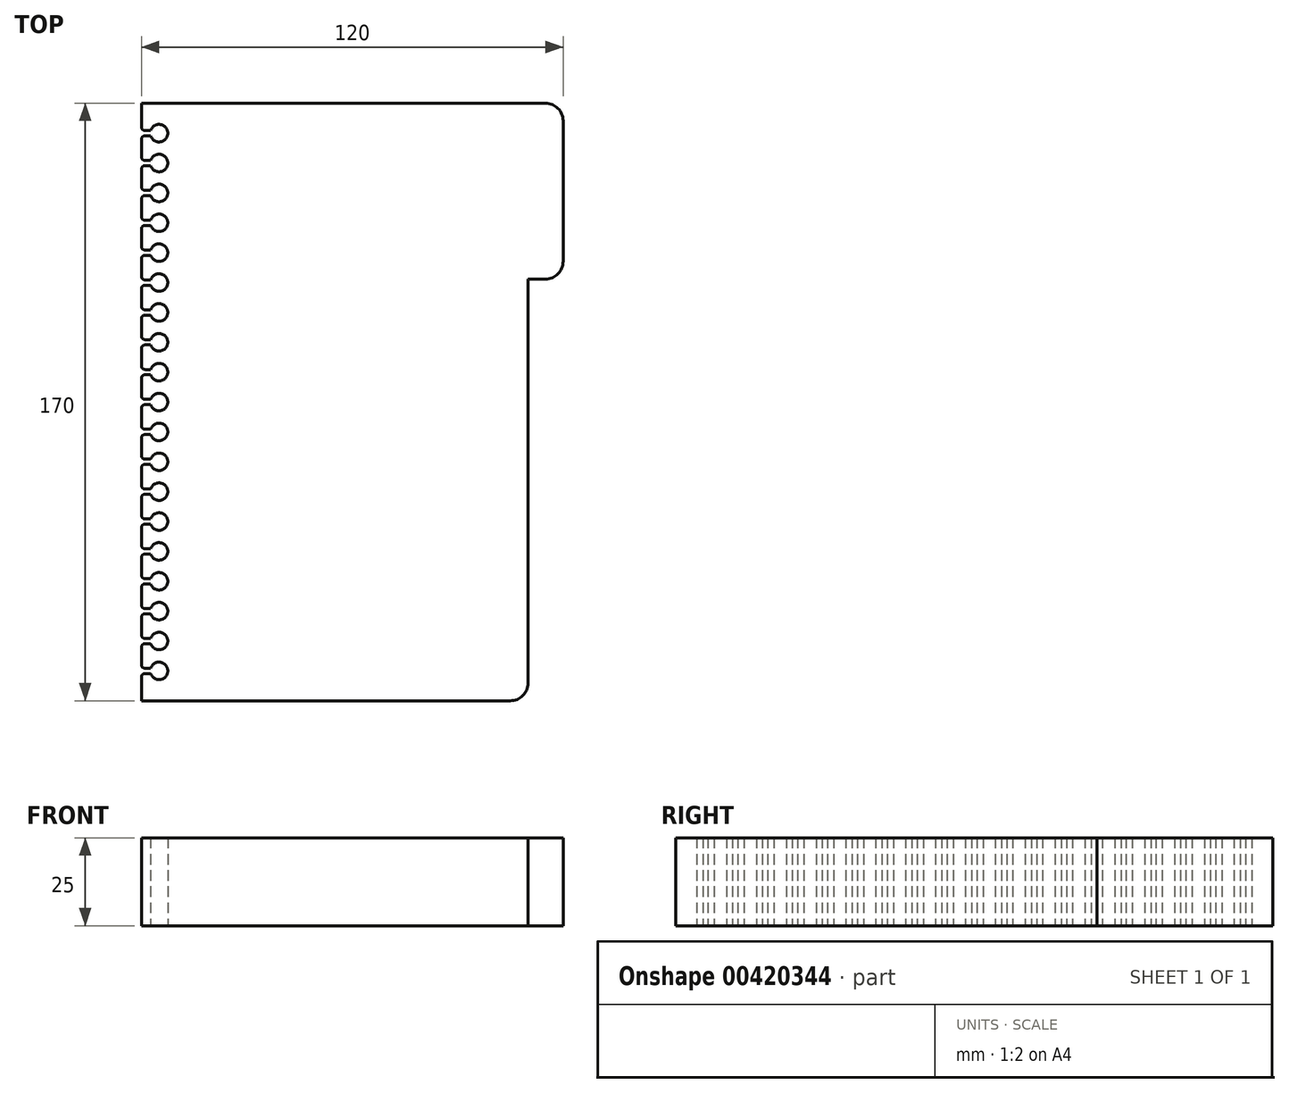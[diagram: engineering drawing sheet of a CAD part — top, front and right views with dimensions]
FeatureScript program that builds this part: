
annotation { "Feature Type Name" : "Feature", "Feature Type Description" : "" }
export const myFeature = defineFeature(function(context is Context, id is Id, definition is map)
    precondition{}
    {
        {
            var Q0;
            Q0=qCreatedBy(makeId("Top.planeOp"),FACE);
            var sketch = newSketch(context, id + "F0", { "sketchPlane" : qUnion([Q0])});
            skLineSegment(sketch, "E0.bottom", {"start": v(-55, 85) * mm, "end": v(50, 85) * mm});
            skLineSegment(sketch, "E0.top", {"start": v(-55, -85) * mm, "end": v(50, -85) * mm});
            skLineSegment(sketch, "E0.left", {"start": v(-55, 85) * mm, "end": v(-55, -74.75) * mm});
            skLineSegment(sketch, "E0.right", {"start": v(55, 80) * mm, "end": v(55, -80) * mm});
            skPoint(sketch, "E0.middle", {"position": v(0, 0) * mm});
            skLineSegment(sketch, "E1", {"start": v(-50, 85) * mm, "end": v(-50, -85) * mm, "construction": true});
            skArc(sketch, "E2", {"start": v(-52.38, -77.25) * mm, "mid": v(-47.5, -76.5) * mm, "end": v(-52.38, -75.75) * mm});
            skLineSegment(sketch, "E3", {"start": v(-52.38, -75.75) * mm, "end": v(-54, -75.75) * mm});
            skLineSegment(sketch, "E4", {"start": v(-50, -76.5) * mm, "end": v(-55, -76.5) * mm, "construction": true});
            skLineSegment(sketch, "E5.MirrorCS", {"start": v(-52.38, -77.25) * mm, "end": v(-54, -77.25) * mm});
            skLineSegment(sketch, "E6.trimOffspring", {"start": v(-55, -78.25) * mm, "end": v(-55, -85) * mm});
            skPoint(sketch, "E7.visualSharp", {"position": v(-55, -75.75) * mm});
            skArc(sketch, "E7.filletArc", {"start": v(-55, -74.75) * mm, "mid": v(-54.7, -75.46) * mm, "end": v(-54, -75.75) * mm});
            skPoint(sketch, "E8.visualSharp", {"position": v(-55, -77.25) * mm});
            skArc(sketch, "E8.filletArc", {"start": v(-54, -77.25) * mm, "mid": v(-54.7, -77.54) * mm, "end": v(-55, -78.25) * mm});
            skPoint(sketch, "E9.0.1.0", {"position": v(-55, -67.25) * mm});
            skPoint(sketch, "E9.0.1.1", {"position": v(-55, -68.75) * mm});
            skLineSegment(sketch, "E9.0.1.2", {"start": v(-52.38, -68.75) * mm, "end": v(-54, -68.75) * mm});
            skLineSegment(sketch, "E9.0.1.3", {"start": v(-50, -68) * mm, "end": v(-55, -68) * mm, "construction": true});
            skLineSegment(sketch, "E9.0.1.4", {"start": v(-52.38, -67.25) * mm, "end": v(-54, -67.25) * mm});
            skArc(sketch, "E9.0.1.5", {"start": v(-52.38, -68.75) * mm, "mid": v(-47.5, -68) * mm, "end": v(-52.38, -67.25) * mm});
            skArc(sketch, "E9.0.1.6", {"start": v(-54, -68.75) * mm, "mid": v(-54.7, -69.04) * mm, "end": v(-55, -69.75) * mm});
            skArc(sketch, "E9.0.1.7", {"start": v(-55, -66.25) * mm, "mid": v(-54.7, -66.96) * mm, "end": v(-54, -67.25) * mm});
            skPoint(sketch, "E9.0.2.0", {"position": v(-55, -58.75) * mm});
            skPoint(sketch, "E9.0.2.1", {"position": v(-55, -60.25) * mm});
            skLineSegment(sketch, "E9.0.2.2", {"start": v(-52.38, -60.25) * mm, "end": v(-54, -60.25) * mm});
            skLineSegment(sketch, "E9.0.2.3", {"start": v(-50, -59.5) * mm, "end": v(-55, -59.5) * mm, "construction": true});
            skLineSegment(sketch, "E9.0.2.4", {"start": v(-52.38, -58.75) * mm, "end": v(-54, -58.75) * mm});
            skArc(sketch, "E9.0.2.5", {"start": v(-52.38, -60.25) * mm, "mid": v(-47.5, -59.5) * mm, "end": v(-52.38, -58.75) * mm});
            skArc(sketch, "E9.0.2.6", {"start": v(-54, -60.25) * mm, "mid": v(-54.7, -60.54) * mm, "end": v(-55, -61.25) * mm});
            skArc(sketch, "E9.0.2.7", {"start": v(-55, -57.75) * mm, "mid": v(-54.7, -58.46) * mm, "end": v(-54, -58.75) * mm});
            skPoint(sketch, "E9.0.3.0", {"position": v(-55, -50.25) * mm});
            skPoint(sketch, "E9.0.3.1", {"position": v(-55, -51.75) * mm});
            skLineSegment(sketch, "E9.0.3.2", {"start": v(-52.38, -51.75) * mm, "end": v(-54, -51.75) * mm});
            skLineSegment(sketch, "E9.0.3.3", {"start": v(-50, -51) * mm, "end": v(-55, -51) * mm, "construction": true});
            skLineSegment(sketch, "E9.0.3.4", {"start": v(-52.38, -50.25) * mm, "end": v(-54, -50.25) * mm});
            skArc(sketch, "E9.0.3.5", {"start": v(-52.38, -51.75) * mm, "mid": v(-47.5, -51) * mm, "end": v(-52.38, -50.25) * mm});
            skArc(sketch, "E9.0.3.6", {"start": v(-54, -51.75) * mm, "mid": v(-54.7, -52.04) * mm, "end": v(-55, -52.75) * mm});
            skArc(sketch, "E9.0.3.7", {"start": v(-55, -49.25) * mm, "mid": v(-54.7, -49.96) * mm, "end": v(-54, -50.25) * mm});
            skPoint(sketch, "E9.0.4.0", {"position": v(-55, -41.75) * mm});
            skPoint(sketch, "E9.0.4.1", {"position": v(-55, -43.25) * mm});
            skLineSegment(sketch, "E9.0.4.2", {"start": v(-52.38, -43.25) * mm, "end": v(-54, -43.25) * mm});
            skLineSegment(sketch, "E9.0.4.3", {"start": v(-50, -42.5) * mm, "end": v(-55, -42.5) * mm, "construction": true});
            skLineSegment(sketch, "E9.0.4.4", {"start": v(-52.38, -41.75) * mm, "end": v(-54, -41.75) * mm});
            skArc(sketch, "E9.0.4.5", {"start": v(-52.38, -43.25) * mm, "mid": v(-47.5, -42.5) * mm, "end": v(-52.38, -41.75) * mm});
            skArc(sketch, "E9.0.4.6", {"start": v(-54, -43.25) * mm, "mid": v(-54.7, -43.54) * mm, "end": v(-55, -44.25) * mm});
            skArc(sketch, "E9.0.4.7", {"start": v(-55, -40.75) * mm, "mid": v(-54.7, -41.46) * mm, "end": v(-54, -41.75) * mm});
            skPoint(sketch, "E9.0.5.0", {"position": v(-55, -33.25) * mm});
            skPoint(sketch, "E9.0.5.1", {"position": v(-55, -34.75) * mm});
            skLineSegment(sketch, "E9.0.5.2", {"start": v(-52.38, -34.75) * mm, "end": v(-54, -34.75) * mm});
            skLineSegment(sketch, "E9.0.5.3", {"start": v(-50, -34) * mm, "end": v(-55, -34) * mm, "construction": true});
            skLineSegment(sketch, "E9.0.5.4", {"start": v(-52.38, -33.25) * mm, "end": v(-54, -33.25) * mm});
            skArc(sketch, "E9.0.5.5", {"start": v(-52.38, -34.75) * mm, "mid": v(-47.5, -34) * mm, "end": v(-52.38, -33.25) * mm});
            skArc(sketch, "E9.0.5.6", {"start": v(-54, -34.75) * mm, "mid": v(-54.7, -35.04) * mm, "end": v(-55, -35.75) * mm});
            skArc(sketch, "E9.0.5.7", {"start": v(-55, -32.25) * mm, "mid": v(-54.7, -32.96) * mm, "end": v(-54, -33.25) * mm});
            skPoint(sketch, "E9.0.6.0", {"position": v(-55, -24.75) * mm});
            skPoint(sketch, "E9.0.6.1", {"position": v(-55, -26.25) * mm});
            skLineSegment(sketch, "E9.0.6.2", {"start": v(-52.38, -26.25) * mm, "end": v(-54, -26.25) * mm});
            skLineSegment(sketch, "E9.0.6.3", {"start": v(-50, -25.5) * mm, "end": v(-55, -25.5) * mm, "construction": true});
            skLineSegment(sketch, "E9.0.6.4", {"start": v(-52.38, -24.75) * mm, "end": v(-54, -24.75) * mm});
            skArc(sketch, "E9.0.6.5", {"start": v(-52.38, -26.25) * mm, "mid": v(-47.5, -25.5) * mm, "end": v(-52.38, -24.75) * mm});
            skArc(sketch, "E9.0.6.6", {"start": v(-54, -26.25) * mm, "mid": v(-54.7, -26.54) * mm, "end": v(-55, -27.25) * mm});
            skArc(sketch, "E9.0.6.7", {"start": v(-55, -23.75) * mm, "mid": v(-54.7, -24.46) * mm, "end": v(-54, -24.75) * mm});
            skPoint(sketch, "E9.0.7.0", {"position": v(-55, -16.25) * mm});
            skPoint(sketch, "E9.0.7.1", {"position": v(-55, -17.75) * mm});
            skLineSegment(sketch, "E9.0.7.2", {"start": v(-52.38, -17.75) * mm, "end": v(-54, -17.75) * mm});
            skLineSegment(sketch, "E9.0.7.3", {"start": v(-50, -17) * mm, "end": v(-55, -17) * mm, "construction": true});
            skLineSegment(sketch, "E9.0.7.4", {"start": v(-52.38, -16.25) * mm, "end": v(-54, -16.25) * mm});
            skArc(sketch, "E9.0.7.5", {"start": v(-52.38, -17.75) * mm, "mid": v(-47.5, -17) * mm, "end": v(-52.38, -16.25) * mm});
            skArc(sketch, "E9.0.7.6", {"start": v(-54, -17.75) * mm, "mid": v(-54.7, -18.04) * mm, "end": v(-55, -18.75) * mm});
            skArc(sketch, "E9.0.7.7", {"start": v(-55, -15.25) * mm, "mid": v(-54.7, -15.96) * mm, "end": v(-54, -16.25) * mm});
            skPoint(sketch, "E9.0.8.0", {"position": v(-55, -7.75) * mm});
            skPoint(sketch, "E9.0.8.1", {"position": v(-55, -9.25) * mm});
            skLineSegment(sketch, "E9.0.8.2", {"start": v(-52.38, -9.25) * mm, "end": v(-54, -9.25) * mm});
            skLineSegment(sketch, "E9.0.8.3", {"start": v(-50, -8.5) * mm, "end": v(-55, -8.5) * mm, "construction": true});
            skLineSegment(sketch, "E9.0.8.4", {"start": v(-52.38, -7.75) * mm, "end": v(-54, -7.75) * mm});
            skArc(sketch, "E9.0.8.5", {"start": v(-52.38, -9.25) * mm, "mid": v(-47.5, -8.5) * mm, "end": v(-52.38, -7.75) * mm});
            skArc(sketch, "E9.0.8.6", {"start": v(-54, -9.25) * mm, "mid": v(-54.7, -9.54) * mm, "end": v(-55, -10.25) * mm});
            skArc(sketch, "E9.0.8.7", {"start": v(-55, -6.75) * mm, "mid": v(-54.7, -7.46) * mm, "end": v(-54, -7.75) * mm});
            skPoint(sketch, "E9.0.9.0", {"position": v(-55, 0.75) * mm});
            skPoint(sketch, "E9.0.9.1", {"position": v(-55, -0.75) * mm});
            skLineSegment(sketch, "E9.0.9.2", {"start": v(-52.38, -0.75) * mm, "end": v(-54, -0.75) * mm});
            skLineSegment(sketch, "E9.0.9.3", {"start": v(-50, 0) * mm, "end": v(-55, 0) * mm, "construction": true});
            skLineSegment(sketch, "E9.0.9.4", {"start": v(-52.38, 0.75) * mm, "end": v(-54, 0.75) * mm});
            skArc(sketch, "E9.0.9.5", {"start": v(-52.38, -0.75) * mm, "mid": v(-47.5, 0) * mm, "end": v(-52.38, 0.75) * mm});
            skArc(sketch, "E9.0.9.6", {"start": v(-54, -0.75) * mm, "mid": v(-54.7, -1.04) * mm, "end": v(-55, -1.75) * mm});
            skArc(sketch, "E9.0.9.7", {"start": v(-55, 1.75) * mm, "mid": v(-54.7, 1.04) * mm, "end": v(-54, 0.75) * mm});
            skPoint(sketch, "E9.0.10.0", {"position": v(-55, 9.25) * mm});
            skPoint(sketch, "E9.0.10.1", {"position": v(-55, 7.75) * mm});
            skLineSegment(sketch, "E9.0.10.2", {"start": v(-52.38, 7.75) * mm, "end": v(-54, 7.75) * mm});
            skLineSegment(sketch, "E9.0.10.3", {"start": v(-50, 8.5) * mm, "end": v(-55, 8.5) * mm, "construction": true});
            skLineSegment(sketch, "E9.0.10.4", {"start": v(-52.38, 9.25) * mm, "end": v(-54, 9.25) * mm});
            skArc(sketch, "E9.0.10.5", {"start": v(-52.38, 7.75) * mm, "mid": v(-47.5, 8.5) * mm, "end": v(-52.38, 9.25) * mm});
            skArc(sketch, "E9.0.10.6", {"start": v(-54, 7.75) * mm, "mid": v(-54.7, 7.46) * mm, "end": v(-55, 6.75) * mm});
            skArc(sketch, "E9.0.10.7", {"start": v(-55, 10.25) * mm, "mid": v(-54.7, 9.54) * mm, "end": v(-54, 9.25) * mm});
            skPoint(sketch, "E9.0.11.0", {"position": v(-55, 17.75) * mm});
            skPoint(sketch, "E9.0.11.1", {"position": v(-55, 16.25) * mm});
            skLineSegment(sketch, "E9.0.11.2", {"start": v(-52.38, 16.25) * mm, "end": v(-54, 16.25) * mm});
            skLineSegment(sketch, "E9.0.11.3", {"start": v(-50, 17) * mm, "end": v(-55, 17) * mm, "construction": true});
            skLineSegment(sketch, "E9.0.11.4", {"start": v(-52.38, 17.75) * mm, "end": v(-54, 17.75) * mm});
            skArc(sketch, "E9.0.11.5", {"start": v(-52.38, 16.25) * mm, "mid": v(-47.5, 17) * mm, "end": v(-52.38, 17.75) * mm});
            skArc(sketch, "E9.0.11.6", {"start": v(-54, 16.25) * mm, "mid": v(-54.7, 15.96) * mm, "end": v(-55, 15.25) * mm});
            skArc(sketch, "E9.0.11.7", {"start": v(-55, 18.75) * mm, "mid": v(-54.7, 18.04) * mm, "end": v(-54, 17.75) * mm});
            skPoint(sketch, "E9.0.12.0", {"position": v(-55, 26.25) * mm});
            skPoint(sketch, "E9.0.12.1", {"position": v(-55, 24.75) * mm});
            skLineSegment(sketch, "E9.0.12.2", {"start": v(-52.38, 24.75) * mm, "end": v(-54, 24.75) * mm});
            skLineSegment(sketch, "E9.0.12.3", {"start": v(-50, 25.5) * mm, "end": v(-55, 25.5) * mm, "construction": true});
            skLineSegment(sketch, "E9.0.12.4", {"start": v(-52.38, 26.25) * mm, "end": v(-54, 26.25) * mm});
            skArc(sketch, "E9.0.12.5", {"start": v(-52.38, 24.75) * mm, "mid": v(-47.5, 25.5) * mm, "end": v(-52.38, 26.25) * mm});
            skArc(sketch, "E9.0.12.6", {"start": v(-54, 24.75) * mm, "mid": v(-54.7, 24.46) * mm, "end": v(-55, 23.75) * mm});
            skArc(sketch, "E9.0.12.7", {"start": v(-55, 27.25) * mm, "mid": v(-54.7, 26.54) * mm, "end": v(-54, 26.25) * mm});
            skPoint(sketch, "E9.0.13.0", {"position": v(-55, 34.75) * mm});
            skPoint(sketch, "E9.0.13.1", {"position": v(-55, 33.25) * mm});
            skLineSegment(sketch, "E9.0.13.2", {"start": v(-52.38, 33.25) * mm, "end": v(-54, 33.25) * mm});
            skLineSegment(sketch, "E9.0.13.3", {"start": v(-50, 34) * mm, "end": v(-55, 34) * mm, "construction": true});
            skLineSegment(sketch, "E9.0.13.4", {"start": v(-52.38, 34.75) * mm, "end": v(-54, 34.75) * mm});
            skArc(sketch, "E9.0.13.5", {"start": v(-52.38, 33.25) * mm, "mid": v(-47.5, 34) * mm, "end": v(-52.38, 34.75) * mm});
            skArc(sketch, "E9.0.13.6", {"start": v(-54, 33.25) * mm, "mid": v(-54.7, 32.96) * mm, "end": v(-55, 32.25) * mm});
            skArc(sketch, "E9.0.13.7", {"start": v(-55, 35.75) * mm, "mid": v(-54.7, 35.04) * mm, "end": v(-54, 34.75) * mm});
            skPoint(sketch, "E9.0.14.0", {"position": v(-55, 43.25) * mm});
            skPoint(sketch, "E9.0.14.1", {"position": v(-55, 41.75) * mm});
            skLineSegment(sketch, "E9.0.14.2", {"start": v(-52.38, 41.75) * mm, "end": v(-54, 41.75) * mm});
            skLineSegment(sketch, "E9.0.14.3", {"start": v(-50, 42.5) * mm, "end": v(-55, 42.5) * mm, "construction": true});
            skLineSegment(sketch, "E9.0.14.4", {"start": v(-52.38, 43.25) * mm, "end": v(-54, 43.25) * mm});
            skArc(sketch, "E9.0.14.5", {"start": v(-52.38, 41.75) * mm, "mid": v(-47.5, 42.5) * mm, "end": v(-52.38, 43.25) * mm});
            skArc(sketch, "E9.0.14.6", {"start": v(-54, 41.75) * mm, "mid": v(-54.7, 41.46) * mm, "end": v(-55, 40.75) * mm});
            skArc(sketch, "E9.0.14.7", {"start": v(-55, 44.25) * mm, "mid": v(-54.7, 43.54) * mm, "end": v(-54, 43.25) * mm});
            skPoint(sketch, "E9.0.15.0", {"position": v(-55, 51.75) * mm});
            skPoint(sketch, "E9.0.15.1", {"position": v(-55, 50.25) * mm});
            skLineSegment(sketch, "E9.0.15.2", {"start": v(-52.38, 50.25) * mm, "end": v(-54, 50.25) * mm});
            skLineSegment(sketch, "E9.0.15.3", {"start": v(-50, 51) * mm, "end": v(-55, 51) * mm, "construction": true});
            skLineSegment(sketch, "E9.0.15.4", {"start": v(-52.38, 51.75) * mm, "end": v(-54, 51.75) * mm});
            skArc(sketch, "E9.0.15.5", {"start": v(-52.38, 50.25) * mm, "mid": v(-47.5, 51) * mm, "end": v(-52.38, 51.75) * mm});
            skArc(sketch, "E9.0.15.6", {"start": v(-54, 50.25) * mm, "mid": v(-54.7, 49.96) * mm, "end": v(-55, 49.25) * mm});
            skArc(sketch, "E9.0.15.7", {"start": v(-55, 52.75) * mm, "mid": v(-54.7, 52.04) * mm, "end": v(-54, 51.75) * mm});
            skPoint(sketch, "E9.0.16.0", {"position": v(-55, 60.25) * mm});
            skPoint(sketch, "E9.0.16.1", {"position": v(-55, 58.75) * mm});
            skLineSegment(sketch, "E9.0.16.2", {"start": v(-52.38, 58.75) * mm, "end": v(-54, 58.75) * mm});
            skLineSegment(sketch, "E9.0.16.3", {"start": v(-50, 59.5) * mm, "end": v(-55, 59.5) * mm, "construction": true});
            skLineSegment(sketch, "E9.0.16.4", {"start": v(-52.38, 60.25) * mm, "end": v(-54, 60.25) * mm});
            skArc(sketch, "E9.0.16.5", {"start": v(-52.38, 58.75) * mm, "mid": v(-47.5, 59.5) * mm, "end": v(-52.38, 60.25) * mm});
            skArc(sketch, "E9.0.16.6", {"start": v(-54, 58.75) * mm, "mid": v(-54.7, 58.46) * mm, "end": v(-55, 57.75) * mm});
            skArc(sketch, "E9.0.16.7", {"start": v(-55, 61.25) * mm, "mid": v(-54.7, 60.54) * mm, "end": v(-54, 60.25) * mm});
            skPoint(sketch, "E9.0.17.0", {"position": v(-55, 68.75) * mm});
            skPoint(sketch, "E9.0.17.1", {"position": v(-55, 67.25) * mm});
            skLineSegment(sketch, "E9.0.17.2", {"start": v(-52.38, 67.25) * mm, "end": v(-54, 67.25) * mm});
            skLineSegment(sketch, "E9.0.17.3", {"start": v(-50, 68) * mm, "end": v(-55, 68) * mm, "construction": true});
            skLineSegment(sketch, "E9.0.17.4", {"start": v(-52.38, 68.75) * mm, "end": v(-54, 68.75) * mm});
            skArc(sketch, "E9.0.17.5", {"start": v(-52.38, 67.25) * mm, "mid": v(-47.5, 68) * mm, "end": v(-52.38, 68.75) * mm});
            skArc(sketch, "E9.0.17.6", {"start": v(-54, 67.25) * mm, "mid": v(-54.7, 66.96) * mm, "end": v(-55, 66.25) * mm});
            skArc(sketch, "E9.0.17.7", {"start": v(-55, 69.75) * mm, "mid": v(-54.7, 69.04) * mm, "end": v(-54, 68.75) * mm});
            skPoint(sketch, "E9.0.18.0", {"position": v(-55, 77.25) * mm});
            skPoint(sketch, "E9.0.18.1", {"position": v(-55, 75.75) * mm});
            skLineSegment(sketch, "E9.0.18.2", {"start": v(-52.38, 75.75) * mm, "end": v(-54, 75.75) * mm});
            skLineSegment(sketch, "E9.0.18.3", {"start": v(-50, 76.5) * mm, "end": v(-55, 76.5) * mm, "construction": true});
            skLineSegment(sketch, "E9.0.18.4", {"start": v(-52.38, 77.25) * mm, "end": v(-54, 77.25) * mm});
            skArc(sketch, "E9.0.18.5", {"start": v(-52.38, 75.75) * mm, "mid": v(-47.5, 76.5) * mm, "end": v(-52.38, 77.25) * mm});
            skArc(sketch, "E9.0.18.6", {"start": v(-54, 75.75) * mm, "mid": v(-54.7, 75.46) * mm, "end": v(-55, 74.75) * mm});
            skArc(sketch, "E9.0.18.7", {"start": v(-55, 78.25) * mm, "mid": v(-54.7, 77.54) * mm, "end": v(-54, 77.25) * mm});
            skLineSegment(sketch, "E9.direction1", {"start": v(-55, -78.25) * mm, "end": v(-30, -78.25) * mm, "construction": true});
            skLineSegment(sketch, "E9.direction2", {"start": v(-55, -78.25) * mm, "end": v(-55, -69.75) * mm, "construction": true});
            skPoint(sketch, "E10.visualSharp", {"position": v(55, 85) * mm});
            skArc(sketch, "E10.filletArc", {"start": v(55, 80) * mm, "mid": v(53.54, 83.54) * mm, "end": v(50, 85) * mm});
            skPoint(sketch, "E11.visualSharp", {"position": v(55, -85) * mm});
            skArc(sketch, "E11.filletArc", {"start": v(50, -85) * mm, "mid": v(53.54, -83.54) * mm, "end": v(55, -80) * mm});
            skLineSegment(sketch, "E12", {"start": v(50, 85) * mm, "end": v(60, 85) * mm});
            skLineSegment(sketch, "E13", {"start": v(65, 80) * mm, "end": v(65, 40) * mm});
            skLineSegment(sketch, "E14", {"start": v(60, 35) * mm, "end": v(55, 35) * mm});
            skPoint(sketch, "E15.visualSharp", {"position": v(65, 85) * mm});
            skArc(sketch, "E15.filletArc", {"start": v(65, 80) * mm, "mid": v(63.54, 83.54) * mm, "end": v(60, 85) * mm});
            skPoint(sketch, "E16.visualSharp", {"position": v(65, 35) * mm});
            skArc(sketch, "E16.filletArc", {"start": v(60, 35) * mm, "mid": v(63.54, 36.46) * mm, "end": v(65, 40) * mm});
            skSolve(sketch);
        }
        {
            var Q0;
            {var subQ28=sQuery(id+"F0.wireOp",EDGE,"E0.bottom");Q0=makeQuery(id+"F0.imprint","IMPRINT",FACE,{"disambiguationData":[TD([[makeQuery(id+"F0.imprint","IMPRINT",EDGE,{"derivedFrom":subQ28}),-1.0]])]});}
            var Q1;
            {var subQ0=sQuery(id+"F0.wireOp",EDGE,"E10.filletArc");Q1=makeQuery(id+"F0.imprint","IMPRINT",FACE,{"disambiguationData":[TD([[makeQuery(id+"F0.imprint","IMPRINT",EDGE,{"derivedFrom":subQ0}),-1.0]])]});}
            extrude(context, id + "F1", {"entities" : qUnion([Q0, Q1]), "depth" : 25 * mm});
        }
    });
